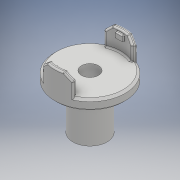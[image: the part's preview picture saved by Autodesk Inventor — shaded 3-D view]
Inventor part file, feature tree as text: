
AUTODESK INVENTOR PART (.ipt)
format: ipt  version: 2018 (Build 220112000, 112)  size: 5,336,576 bytes
history: native  units: mm
features: extrude x14, sketch x14, other x9, mirror x3, pattern_circular x3, fillet x3, projected_geometry x3, chamfer x2
ambient origin geometry x8: Origin, YZ Plane, XZ Plane, XY Plane, X Axis, Y Axis, Z Axis, Center Point
bodies: Body1 (feature_tree)
feature tree (51):
  other  "gear.ipt"
  other  "ソリッド1"
  extrude  "押し出し1"  Depth=33.0mm
  extrude  "押し出し2"  Depth=20.0mm TaperAngle=0.0deg
  mirror  "ミラー1"
  extrude  "押し出し3"  Depth=2.0mm
  mirror  "ミラー2"
  extrude  "押し出し4"  Depth=14.5mm
  mirror  "ミラー3"
  other  "結合1"
  extrude  "押し出し5"  Depth=9.2mm TaperAngle=0.0deg
  extrude  "押し出し6"  Depth=7.5mm
  pattern_circular  "円形状パターン1"  [2 undecoded]
  fillet  "フィレット1"  Radius=9.2mm
  fillet  "フィレット2"  Radius=2.5mm
  extrude  "押し出し7"  Depth=1.0mm
  chamfer  "面取り2"  Distance=1.0mm
  extrude  "押し出し8"  Depth=4.0mm TaperAngle=0.0deg
  extrude  "押し出し9"  Depth=10.0mm
  extrude  "押し出し10"  Depth=4.0mm TaperAngle=0.0deg
  extrude  "押し出し11"  TaperAngle=45.0deg  [1 undecoded]
  fillet  "フィレット3"  Radius=0.2mm
  extrude  "押し出し12"  Depth=0.2mm
  chamfer  "面取り3"  Angle=45.0deg  [1 undecoded]
  pattern_circular  "円形状パターン2"  [2 undecoded]
  extrude  "押し出し13"  Depth=220.0mm TaperAngle=360.0deg
  pattern_circular  "円形状パターン3"  [2 undecoded]
  extrude  "押し出し14"  Depth=0.5mm
  sketch  "スケッチ1"
  sketch  "スケッチ2"
  sketch  "スケッチ3"
  sketch  "スケッチ4"
  other  "ソリッド1::gear.ipt"
  other  "TaggingFeature1"
  sketch  "スケッチ6"
  projected_geometry  "投影ループ1"
  sketch  "スケッチ7"
  projected_geometry  "投影ループ2"
  sketch  "スケッチ8"
  sketch  "スケッチ9"
  sketch  "スケッチ10"
  projected_geometry  "投影ループ3"
  sketch  "スケッチ12"
  sketch  "スケッチ14"
  sketch  "スケッチ15"
  sketch  "スケッチ16"
  sketch  "スケッチ17"
  other  "ソリッド2"
  other  "断面エッジを投影1"
  other  "断面エッジを投影2"
  other  "断面エッジを投影3"
note: 8 required parameter values undecoded (feature->parameter linkage not recoverable at this tier; creation-order binding heuristic only, values carry confidence <= 0.55)
